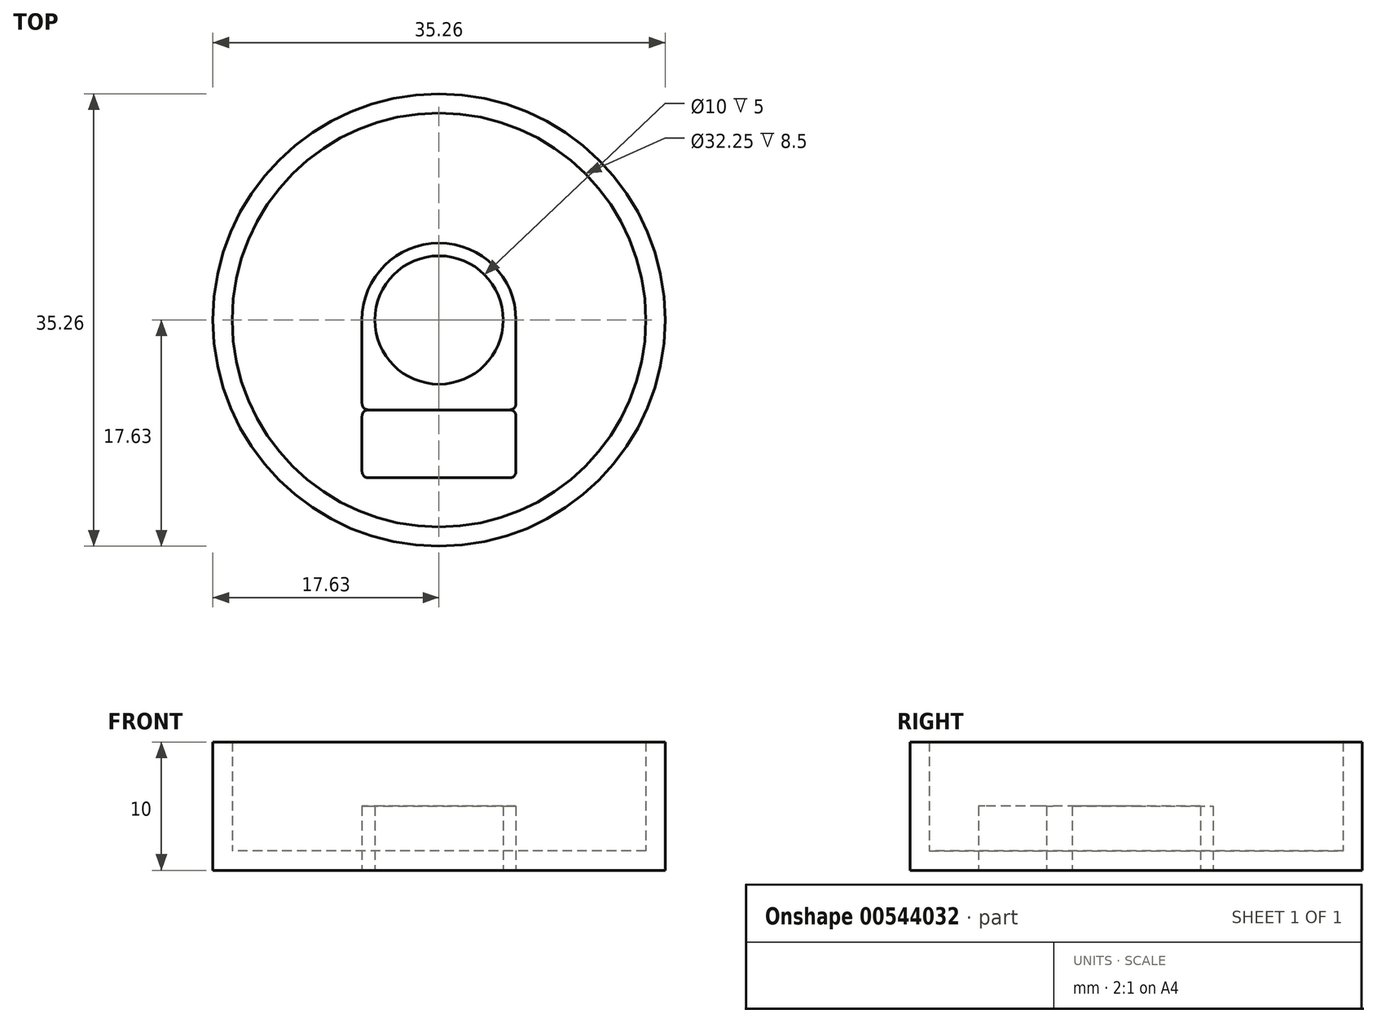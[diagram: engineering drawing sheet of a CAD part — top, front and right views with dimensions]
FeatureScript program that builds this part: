
annotation { "Feature Type Name" : "Feature", "Feature Type Description" : "" }
export const myFeature = defineFeature(function(context is Context, id is Id, definition is map)
    precondition{}
    {
        {
            var Q0;
            Q0=qCreatedBy(makeId("Top.planeOp"),FACE);
            var sketch = newSketch(context, id + "F0", { "sketchPlane" : qUnion([Q0])});
            skCircle(sketch, "E0", {"center": v(0, 0) * mm, "radius": 17.62 * mm});
            skCircle(sketch, "E1", {"center": v(0, 0) * mm, "radius": 16.12 * mm});
            skSolve(sketch);
        }
        {
            var Q0;
            Q0=makeQuery(id+"F0.imprint","IMPRINT",FACE,{"disambiguationData":[TD([[makeQuery(id+"F0.imprint","IMPRINT",EDGE,{"derivedFrom":sQuery(id+"F0.wireOp",EDGE,"E0")}),1.0]])]});
            var Q1;
            Q1=makeQuery(id+"F0.imprint","IMPRINT",FACE,{"disambiguationData":[TD([[makeQuery(id+"F0.imprint","IMPRINT",EDGE,{"derivedFrom":sQuery(id+"F0.wireOp",EDGE,"E1")}),1.0]])]});
            extrude(context, id + "F1", {"entities" : qUnion([Q0, Q1]), "depth" : 1.5 * mm, "offsetDistance" : 25 * mm});
        }
        {
            var Q0;
            Q0=makeQuery(id+"F0.imprint","IMPRINT",FACE,{"disambiguationData":[TD([[makeQuery(id+"F0.imprint","IMPRINT",EDGE,{"derivedFrom":sQuery(id+"F0.wireOp",EDGE,"E0")}),1.0]])]});
            extrude(context, id + "F2", {"entities" : qUnion([Q0]), "operationType" : NewBodyOperationType.ADD, "depth" : 10 * mm, "offsetDistance" : 25 * mm});
        }
        {
            var Q0;
            Q0=qCreatedBy(makeId("Top.planeOp"),FACE);
            var sketch = newSketch(context, id + "F3", { "sketchPlane" : qUnion([Q0])});
            skCircle(sketch, "E2", {"center": v(0, 0) * mm, "radius": 6 * mm});
            skLineSegment(sketch, "E3.bottom", {"start": v(-6, 0) * mm, "end": v(6, 0) * mm});
            skLineSegment(sketch, "E3.top", {"start": v(-6, -7) * mm, "end": v(6, -7) * mm});
            skLineSegment(sketch, "E3.left", {"start": v(-6, 0) * mm, "end": v(-6, -7) * mm});
            skLineSegment(sketch, "E3.right", {"start": v(6, 0) * mm, "end": v(6, -7) * mm});
            skCircle(sketch, "E4", {"center": v(0, 0) * mm, "radius": 5 * mm});
            skLineSegment(sketch, "E5.top", {"start": v(-6, -12.3) * mm, "end": v(6, -12.3) * mm});
            skLineSegment(sketch, "E5.left", {"start": v(-6, -7) * mm, "end": v(-6, -12.3) * mm});
            skLineSegment(sketch, "E5.right", {"start": v(6, -7) * mm, "end": v(6, -12.3) * mm});
            skSolve(sketch);
        }
        {
            var Q0;
            Q0=makeQuery(id+"F3.imprint","IMPRINT",FACE,{"disambiguationData":[TD([[makeQuery(id+"F3.imprint","IMPRINT",EDGE,{"derivedFrom":sQuery(id+"F3.wireOp",EDGE,"E3.top")}),1.0]])]});
            var Q1;
            {var subQ0=sQuery(id+"F3.wireOp",EDGE,"E3.bottom");var subQ4=sQuery(id+"F3.wireOp",EDGE,"E4");var subQ5=makeQuery(id+"F3.imprint","INTERSECT",VERTEX,{"disambiguationData":[OD(0.0)],"derivedFrom":[subQ0,subQ4]});Q1=makeQuery(id+"F3.imprint","IMPRINT",FACE,{"disambiguationData":[TD([[makeQuery(id+"F3.imprint","IMPRINT",EDGE,{"disambiguationData":[TD([[subQ5,-1.0]])],"derivedFrom":subQ4}),-1.0]])]});}
            var Q2;
            {var subQ0=sQuery(id+"F3.wireOp",EDGE,"E3.bottom");var subQ4=sQuery(id+"F3.wireOp",EDGE,"E4");var subQ5=makeQuery(id+"F3.imprint","INTERSECT",VERTEX,{"disambiguationData":[OD(0.0)],"derivedFrom":[subQ0,subQ4]});Q2=makeQuery(id+"F3.imprint","IMPRINT",FACE,{"disambiguationData":[TD([[makeQuery(id+"F3.imprint","IMPRINT",EDGE,{"disambiguationData":[TD([[subQ5,1.0]])],"derivedFrom":subQ4}),-1.0]])]});}
            var Q3;
            {var subQ0=sQuery(id+"F3.wireOp",EDGE,"E3.left");Q3=makeQuery(id+"F3.imprint","IMPRINT",FACE,{"disambiguationData":[TD([[makeQuery(id+"F3.imprint","IMPRINT",EDGE,{"derivedFrom":subQ0}),1.0]])]});}
            extrude(context, id + "F4", {"entities" : qUnion([Q0, Q1, Q2, Q3]), "depth" : 5 * mm, "offsetDistance" : 25 * mm});
        }
        {
            var Q0;
            Q0=makeQuery(id+"F3.imprint","IMPRINT",FACE,{"disambiguationData":[TD([[makeQuery(id+"F3.imprint","IMPRINT",EDGE,{"derivedFrom":sQuery(id+"F3.wireOp",EDGE,"E3.top")}),-1.0]])]});
            extrude(context, id + "F5", {"entities" : qUnion([Q0]), "depth" : 5 * mm, "offsetDistance" : 25 * mm});
        }
        {
            var Q0;
            Q0=makeQuery(id+"F4.opExtrude","SWEPT_EDGE",EDGE,{"disambiguationData":[OSD([sQuery(id+"F3.wireOp",EDGE,"E3.top"),sQuery(id+"F3.wireOp",EDGE,"E3.left")])]});
            var Q1;
            Q1=makeQuery(id+"F4.opExtrude","SWEPT_EDGE",EDGE,{"disambiguationData":[OSD([sQuery(id+"F3.wireOp",EDGE,"E3.top"),sQuery(id+"F3.wireOp",EDGE,"E3.right")])]});
            var Q2;
            Q2=makeQuery(id+"F5.opExtrude","SWEPT_EDGE",EDGE,{"disambiguationData":[OSD([sQuery(id+"F3.wireOp",EDGE,"E5.top"),sQuery(id+"F3.wireOp",EDGE,"E5.right")])]});
            var Q3;
            Q3=makeQuery(id+"F5.opExtrude","SWEPT_EDGE",EDGE,{"disambiguationData":[OSD([sQuery(id+"F3.wireOp",EDGE,"E5.top"),sQuery(id+"F3.wireOp",EDGE,"E5.left")])]});
            var Q4;
            Q4=makeQuery(id+"F5.opExtrude","SWEPT_EDGE",EDGE,{"disambiguationData":[OSD([sQuery(id+"F3.wireOp",EDGE,"E3.right"),sQuery(id+"F3.wireOp",EDGE,"E3.top"),sQuery(id+"F3.wireOp",EDGE,"E5.right")])]});
            var Q5;
            Q5=makeQuery(id+"F5.opExtrude","SWEPT_EDGE",EDGE,{"disambiguationData":[OSD([sQuery(id+"F3.wireOp",EDGE,"E3.left"),sQuery(id+"F3.wireOp",EDGE,"E3.top"),sQuery(id+"F3.wireOp",EDGE,"E5.left")])]});
            fillet(context, id + "F6", {"entities" : qUnion([Q0, Q1, Q2, Q3, Q4, Q5]), "radius" : 0.5 * mm, "tangentPropagation" : true, "allowEdgeOverflow" : false});
        }
    });
